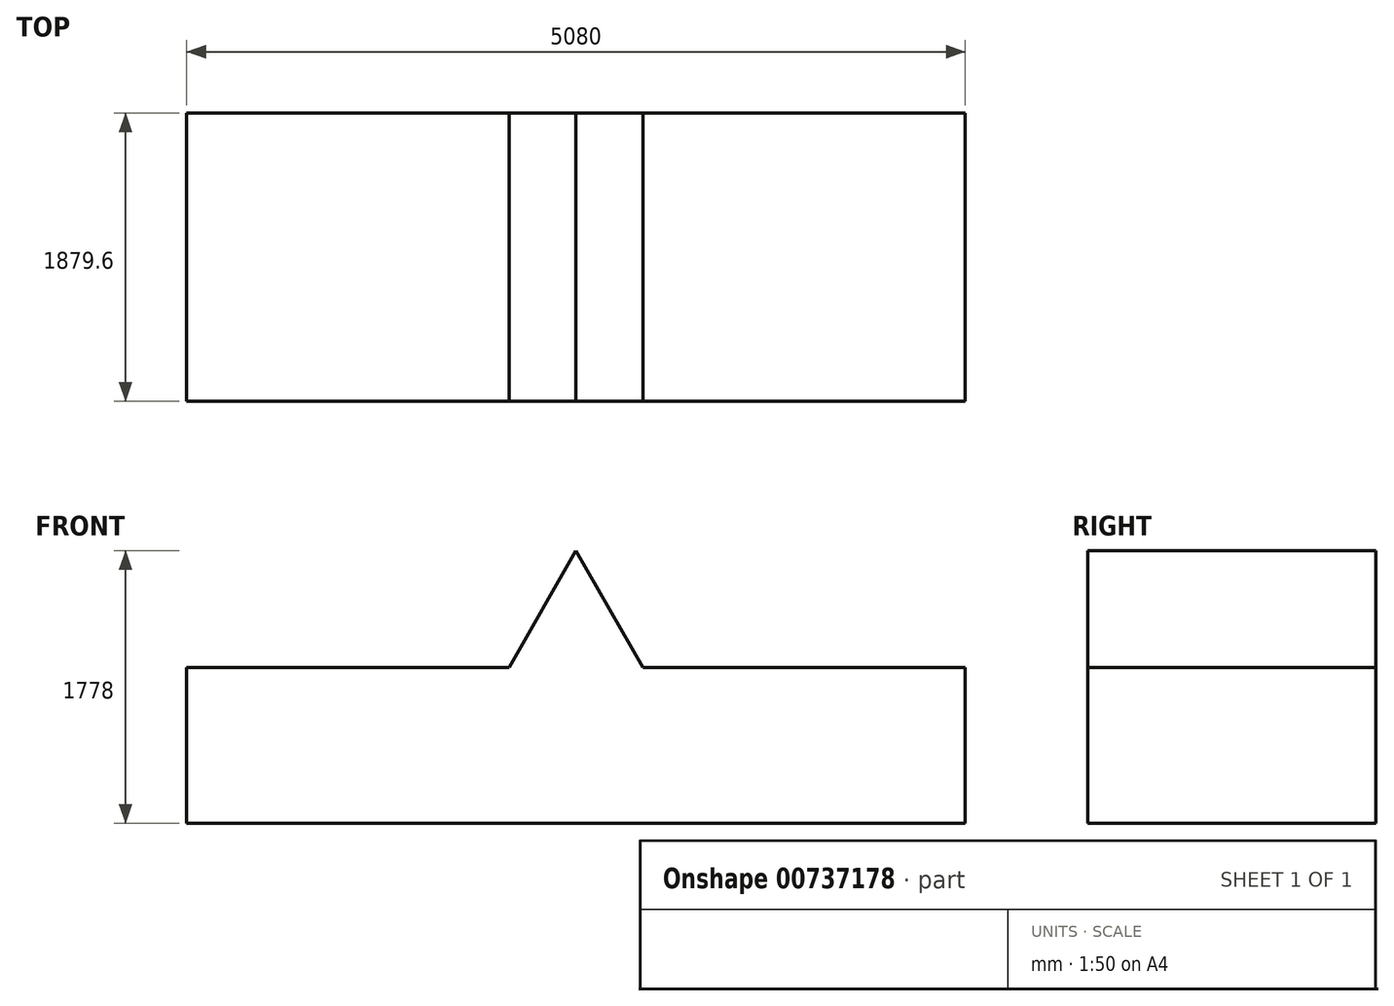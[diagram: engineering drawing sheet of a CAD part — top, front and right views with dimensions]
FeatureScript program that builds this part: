
annotation { "Feature Type Name" : "Feature", "Feature Type Description" : "" }
export const myFeature = defineFeature(function(context is Context, id is Id, definition is map)
    precondition{}
    {
        {
            var Q0;
            Q0=qCreatedBy(makeId("Front.planeOp"),FACE);
            var sketch = newSketch(context, id + "F0", { "sketchPlane" : qUnion([Q0])});
            skLineSegment(sketch, "E0.bottom", {"start": v(-2540, -889) * mm, "end": v(2540, -889) * mm});
            skLineSegment(sketch, "E0.top", {"start": v(-2540, 889) * mm, "end": v(2540, 889) * mm});
            skLineSegment(sketch, "E0.left", {"start": v(-2540, -889) * mm, "end": v(-2540, 889) * mm});
            skLineSegment(sketch, "E0.right", {"start": v(2540, -889) * mm, "end": v(2540, 889) * mm});
            skPoint(sketch, "E0.middle", {"position": v(0, 0) * mm});
            skSolve(sketch);
        }
        {
            var Q0;
            Q0 = qSketchRegion(id + "F0", true);
            extrude(context, id + "F1", {"entities" : qUnion([Q0]), "depth" : 1879.6 * mm, "offsetDistance" : 25.4 * mm});
        }
        {
            var Q0;
            Q0=makeQuery(id+"F1.opExtrude","CAP_FACE",FACE,{"disambiguationData":[OSD([sQuery(id+"F0.wireOp",EDGE,"E0.bottom"),sQuery(id+"F0.wireOp",EDGE,"E0.top"),sQuery(id+"F0.wireOp",EDGE,"E0.left"),sQuery(id+"F0.wireOp",EDGE,"E0.right")])],"isStart":false});
            var sketch = newSketch(context, id + "F2", { "sketchPlane" : qUnion([Q0])});
            skLineSegment(sketch, "E1", {"start": v(-2540, -889) * mm, "end": v(-2540, 127) * mm});
            skLineSegment(sketch, "E2", {"start": v(-2540, 127) * mm, "end": v(2540, 127) * mm});
            skLineSegment(sketch, "E3", {"start": v(2540, 127) * mm, "end": v(2540, 889) * mm});
            skLineSegment(sketch, "E4", {"start": v(2540, 889) * mm, "end": v(-2540, 889) * mm});
            skLineSegment(sketch, "E5", {"start": v(-2540, 889) * mm, "end": v(-2540, 127) * mm});
            skLineSegment(sketch, "E6", {"start": v(0, 889) * mm, "end": v(-1016, -889) * mm});
            skLineSegment(sketch, "E7", {"start": v(0, 889) * mm, "end": v(1016, -889) * mm});
            skLineSegment(sketch, "E8", {"start": v(-2540, -889) * mm, "end": v(-1016, -889) * mm});
            skLineSegment(sketch, "E9", {"start": v(1016, -889) * mm, "end": v(2540, -889) * mm});
            skSolve(sketch);
        }
        {
            var Q0;
            {var subQ0=sQuery(id+"F2.wireOp",EDGE,"E5");Q0=makeQuery(id+"F2.imprint","IMPRINT",FACE,{"disambiguationData":[TD([[makeQuery(id+"F2.imprint","IMPRINT",EDGE,{"derivedFrom":subQ0}),-1.0]])]});}
            var Q1;
            {var subQ0=sQuery(id+"F2.wireOp",EDGE,"E3");Q1=makeQuery(id+"F2.imprint","IMPRINT",FACE,{"disambiguationData":[TD([[makeQuery(id+"F2.imprint","IMPRINT",EDGE,{"derivedFrom":subQ0}),1.0]])]});}
            extrude(context, id + "F3", {"entities" : qUnion([Q0, Q1]), "operationType" : NewBodyOperationType.REMOVE, "oppositeDirection" : true, "depth" : 1879.6 * mm, "offsetDistance" : 25.4 * mm});
        }
    });
